# Revit family: Dallmeier_PTZ_Outdoor_en
name_source: partatom
category: Sicherheitsgeräte
units: mm (PartAtom-declared; Revit-internal decimal feet)

## family parameters
Basisbauteil = Fläche
Beim Laden mit Abzugskörper schneiden = Nein
Bemaßung runder Anschluss = Durchmesser verwenden
Beschriftungsausrichtung beibehalten = Nein
Gemeinsam genutzt = Nein
Raumberechnungspunkt = Nein
Teiletyp = Normal

## types (4) — shared parameters
Hersteller = Dallmeier electronics GmbH
URL = https://www.dallmeier.com
Vorgabe-Ansicht = 122 cm
number of sensors = 1
voltage supply = 48 V

## per-type parameters (varying)
| type | 4:3 Available | DDZ5000HD_DN_IR | DDZ5200HD_Outdoor | Long Horizontal FOV | Modell | Pixel Horizontal 16:9 | Pixel Horizontal 4:3 | Short Horizontal FOV | dimensions | operating temperature | power consumption | weight |
| DDZ 5236 HD-DN/IR | Ja | Ja | Nein | 56,10° | DDZ 5236 HD-DN/IR | 1920 | 1440 | 2,00° | 303x416x303mm | -30°C to +65°C | 60 W | 16,20 kg |
| DDZ 5436 HD-DN/IR | Ja | Ja | Nein | 56,10° | DDZ 5236 HD-DN/IR | 3840 | 2592 | 2,00° | 303x416x303mm | -30°C to +65°C | 60 W | 16,20 kg |
| DDZ 5220 HD Outdoor | Nein | Nein | Ja | 58,00° | DDZ 5220 HD-DN/IR | 1920 | 1440 | 3,00° | 245x322x245mm | -40°C to +55°C | 85 W | 8,80 kg |
| DDZ 5232 HD Outdoor | Nein | Nein | Ja | 61,40° | DDZ 5236 HD-DN/IR | 1920 | 1440 | 2,10° | 245x322x245mm | -40°C to +55°C | 85 W | 8,80 kg |

## geometry (parser evidence)
native form markers: Sweep x56
no freeform markers — native parametric forms only
